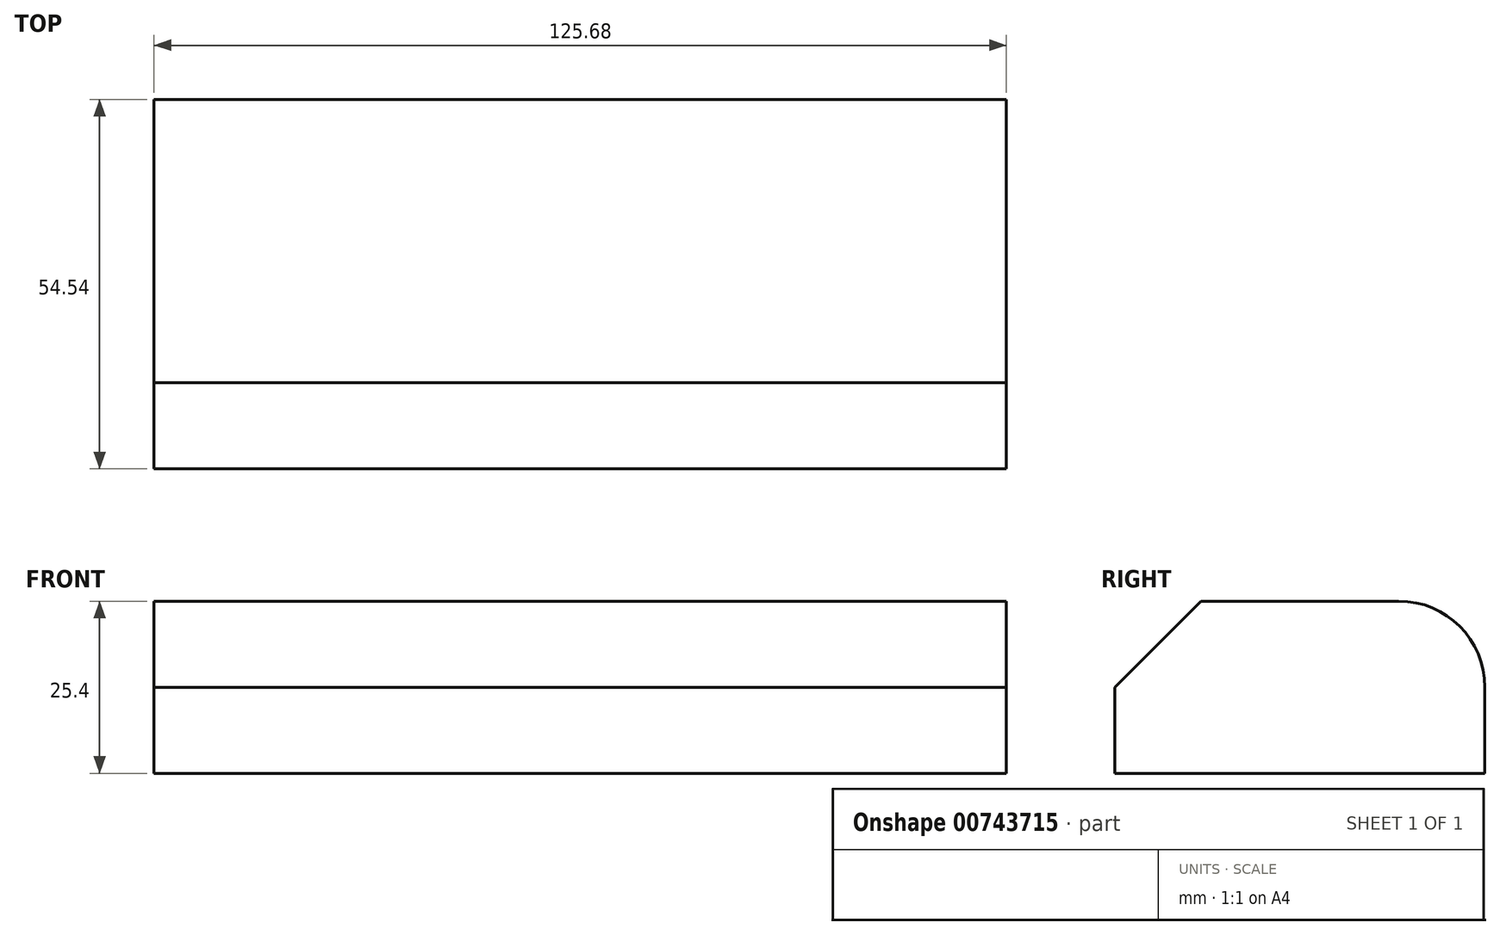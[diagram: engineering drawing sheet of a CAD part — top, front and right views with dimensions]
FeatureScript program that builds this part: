
annotation { "Feature Type Name" : "Feature", "Feature Type Description" : "" }
export const myFeature = defineFeature(function(context is Context, id is Id, definition is map)
    precondition{}
    {
        {
            var Q0;
            Q0=qCreatedBy(makeId("Top.planeOp"),FACE);
            var sketch = newSketch(context, id + "F0", { "sketchPlane" : qUnion([Q0])});
            skLineSegment(sketch, "E0.bottom", {"start": v(-62.84, 27.27) * mm, "end": v(62.84, 27.27) * mm});
            skLineSegment(sketch, "E0.top", {"start": v(-62.84, -27.27) * mm, "end": v(62.84, -27.27) * mm});
            skLineSegment(sketch, "E0.left", {"start": v(-62.84, 27.27) * mm, "end": v(-62.84, -27.27) * mm});
            skLineSegment(sketch, "E0.right", {"start": v(62.84, 27.27) * mm, "end": v(62.84, -27.27) * mm});
            skPoint(sketch, "E0.middle", {"position": v(0, 0) * mm});
            skSolve(sketch);
        }
        {
            var Q0;
            Q0 = qSketchRegion(id + "F0", true);
            extrude(context, id + "F1", {"entities" : qUnion([Q0]), "depth" : 25.4 * mm, "offsetDistance" : 25.4 * mm});
        }
        {
            var Q0;
            Q0=makeQuery(id+"F1.opExtrude","CAP_EDGE",EDGE,{"disambiguationData":[OSD([sQuery(id+"F0.wireOp",EDGE,"E0.top")])],"isStart":false});
            chamfer(context, id + "F2", {"entities" : qUnion([Q0]), "width" : 12.7 * mm, "tangentPropagation" : true});
        }
        {
            var Q0;
            Q0=makeQuery(id+"F1.opExtrude","CAP_EDGE",EDGE,{"disambiguationData":[OSD([sQuery(id+"F0.wireOp",EDGE,"E0.bottom")])],"isStart":false});
            fillet(context, id + "F3", {"entities" : qUnion([Q0]), "radius" : 12.7 * mm, "tangentPropagation" : true, "allowEdgeOverflow" : false});
        }
    });
